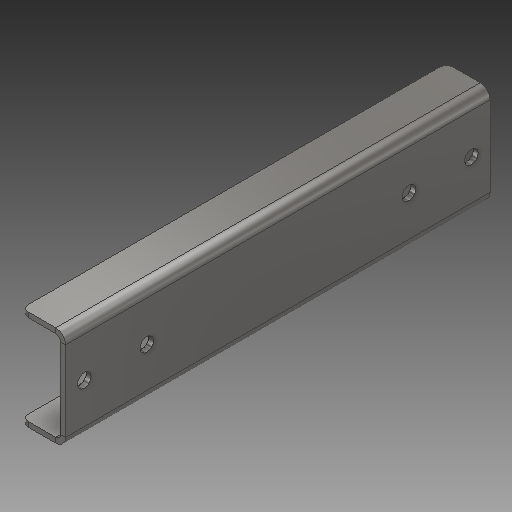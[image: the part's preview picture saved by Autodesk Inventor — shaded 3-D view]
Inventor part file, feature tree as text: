
AUTODESK INVENTOR PART (.ipt)
format: ipt  version: 2017 (Build 210142000, 142)  size: 150,528 bytes
history: native  units: mm
features: sheet_metal_op x3, sketch x2, fillet x1, hole x1, other x1, projected_geometry x1
ambient origin geometry x8: Origin, YZ Plane, XZ Plane, XY Plane, X Axis, Y Axis, Z Axis, Center Point
bodies: Solid1 (feature_tree)
feature tree (9):
  sheet_metal_op  "Contour Flange1"
  fillet  "Fillet1"  Radius=35.0mm
  hole  "Hole1"  [1 undecoded]
  sketch  "Sketch1"  dims[d1=35.0mm d2=80.0mm]
  other  "Plate1"
  sheet_metal_op  "Bend1"
  sheet_metal_op  "Corner1"
  sketch  "Sketch2"  dims[d3=4.0mm d4=2.0mm d5=8.0mm d6=3.9mm d8=3.9mm d9=0.5mm d10=16.0mm d11=4.0mm d12=3.9mm d13=5.0mm d14=15.0mm d15=50.0mm d16=50.0mm d17=15.0mm d18=11.0mm d19=6.0mm d20=3.023mm d21=2.0mm d22=14.3117mm d23=4.0mm d24=20.594885mm]
  projected_geometry  "Projected Loop1"
note: 1 required parameter value undecoded (feature->parameter linkage not recoverable at this tier; creation-order binding heuristic only, values carry confidence <= 0.55)
